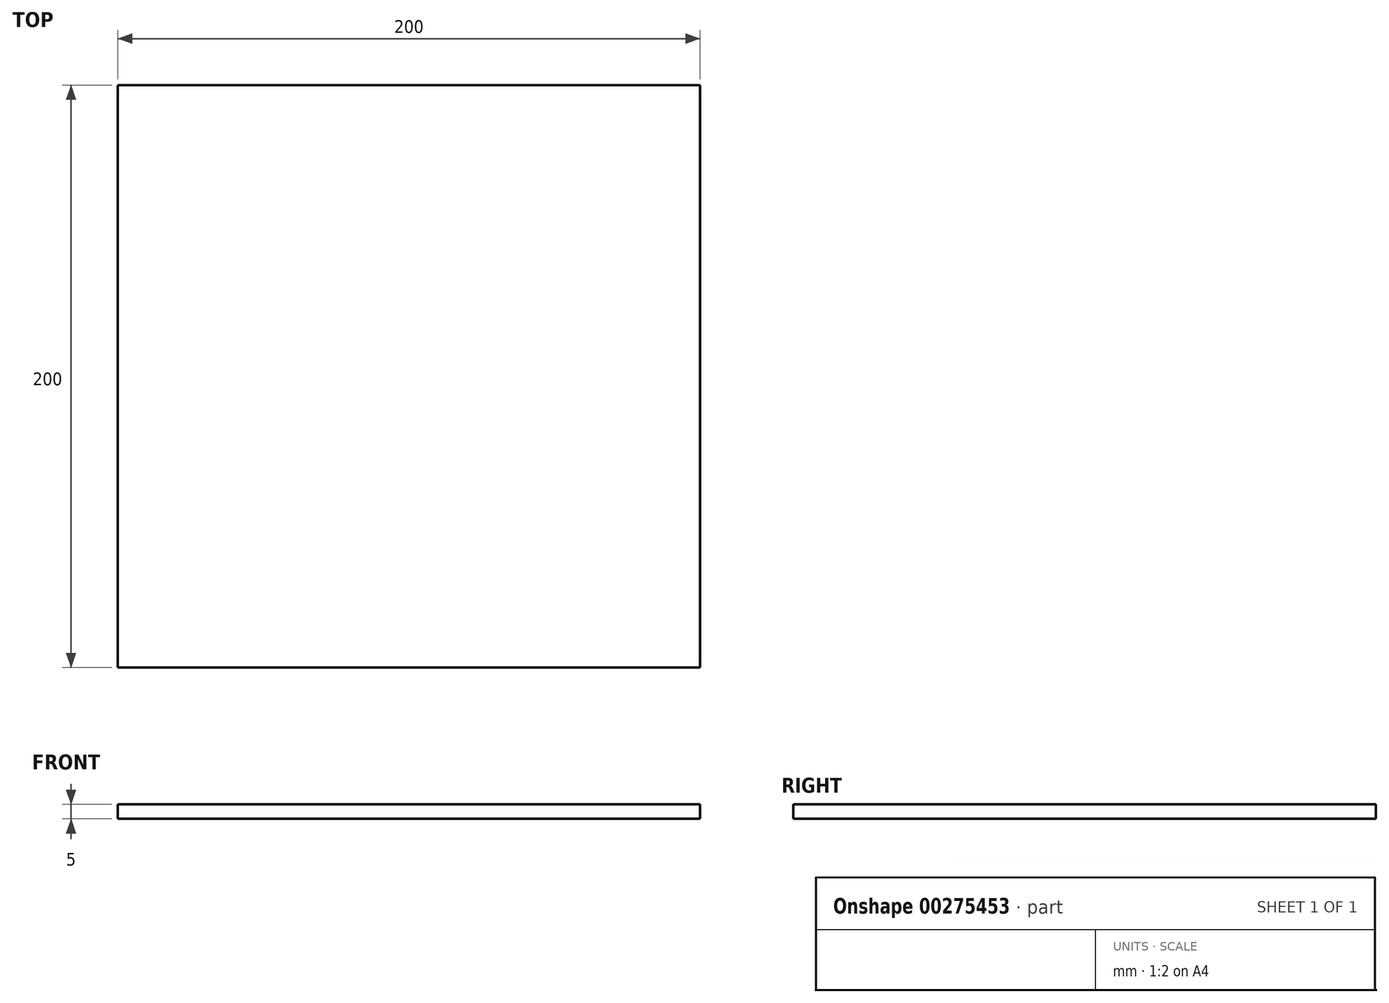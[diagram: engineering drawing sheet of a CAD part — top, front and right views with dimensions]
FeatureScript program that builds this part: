
annotation { "Feature Type Name" : "Feature", "Feature Type Description" : "" }
export const myFeature = defineFeature(function(context is Context, id is Id, definition is map)
    precondition{}
    {
        {
            var Q0;
            Q0=qCreatedBy(makeId("Top.planeOp"),FACE);
            var sketch = newSketch(context, id + "F0", { "sketchPlane" : qUnion([Q0])});
            skLineSegment(sketch, "E0.bottom", {"start": v(100, -100) * mm, "end": v(-100, -100) * mm});
            skLineSegment(sketch, "E0.top", {"start": v(100, 100) * mm, "end": v(-100, 100) * mm});
            skLineSegment(sketch, "E0.left", {"start": v(100, -100) * mm, "end": v(100, 100) * mm});
            skLineSegment(sketch, "E0.right", {"start": v(-100, -100) * mm, "end": v(-100, 100) * mm});
            skPoint(sketch, "E0.middle", {"position": v(0, 0) * mm});
            skSolve(sketch);
        }
        {
            var Q0;
            Q0=qSketchRegion(id+"F0",true);
            extrude(context, id + "F1", {"entities" : qUnion([Q0]), "depth" : 5 * mm});
        }
    });
